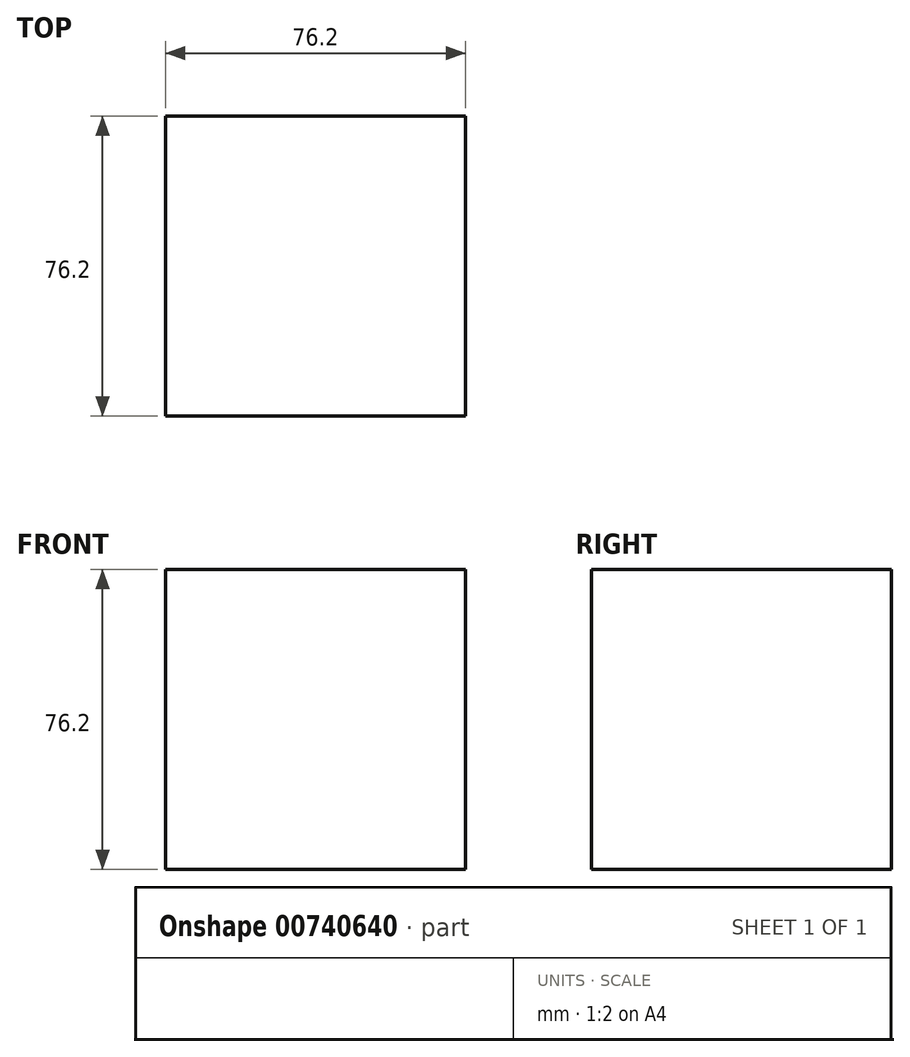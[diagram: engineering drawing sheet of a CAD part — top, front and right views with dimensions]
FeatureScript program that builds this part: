
annotation { "Feature Type Name" : "Feature", "Feature Type Description" : "" }
export const myFeature = defineFeature(function(context is Context, id is Id, definition is map)
    precondition{}
    {
        {
            var Q0;
            Q0=qCreatedBy(makeId("Top.planeOp"),FACE);
            var sketch = newSketch(context, id + "F0", { "sketchPlane" : qUnion([Q0])});
            skLineSegment(sketch, "E0.bottom", {"start": v(38.1, -38.1) * mm, "end": v(-38.1, -38.1) * mm});
            skLineSegment(sketch, "E0.top", {"start": v(38.1, 38.1) * mm, "end": v(-38.1, 38.1) * mm});
            skLineSegment(sketch, "E0.left", {"start": v(38.1, -38.1) * mm, "end": v(38.1, 38.1) * mm});
            skLineSegment(sketch, "E0.right", {"start": v(-38.1, -38.1) * mm, "end": v(-38.1, 38.1) * mm});
            skPoint(sketch, "E0.middle", {"position": v(0, 0) * mm});
            skSolve(sketch);
        }
        {
            var Q0;
            Q0=qCreatedBy(makeId("Top.planeOp"),FACE);
            var sketch = newSketch(context, id + "F1", { "sketchPlane" : qUnion([Q0])});
            skCircle(sketch, "E1", {"center": v(0, 0) * mm, "radius": 23.85 * mm});
            skSolve(sketch);
        }
        {
            var Q0;
            Q0=makeQuery(id+"F0.imprint","IMPRINT",FACE,{"disambiguationData":[TD([[makeQuery(id+"F0.imprint","IMPRINT",EDGE,{"derivedFrom":sQuery(id+"F0.wireOp",EDGE,"E0.bottom")}),-1.0]])]});
            extrude(context, id + "F2", {"entities" : qUnion([Q0]), "depth" : 76.2 * mm, "offsetDistance" : 25.4 * mm});
        }
        {
            var Q0;
            Q0=sQuery(id+"F1.wireOp",EDGE,"E1");
            extrude(context, id + "F3", {"bodyType" : ToolBodyType.SURFACE, "surfaceEntities" : qUnion([Q0]), "oppositeDirection" : true, "depth" : 38.1 * mm, "offsetDistance" : 25.4 * mm});
        }
    });
